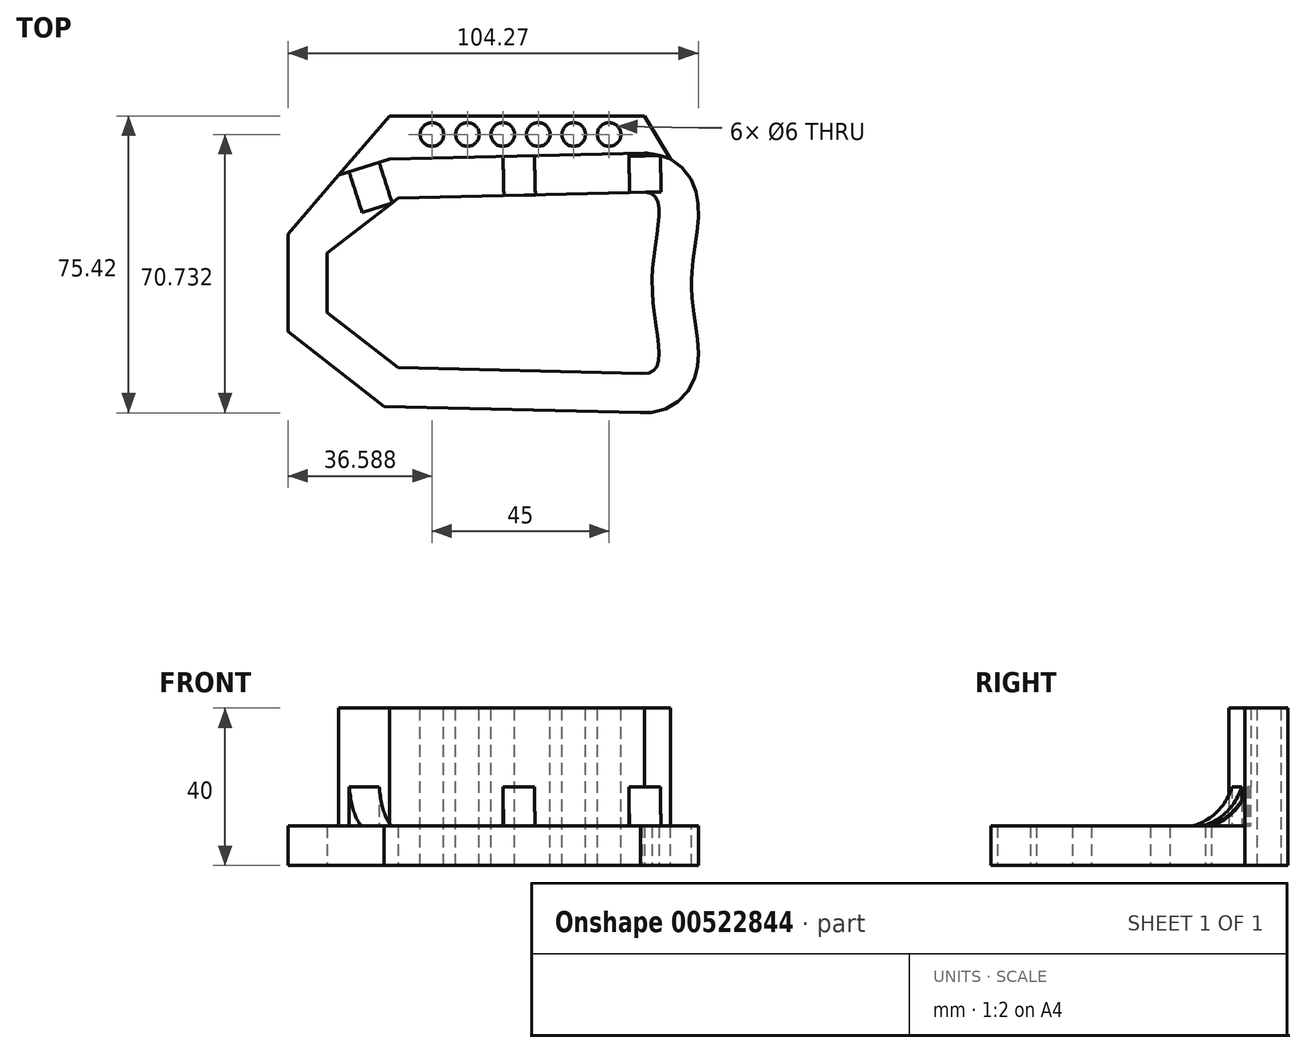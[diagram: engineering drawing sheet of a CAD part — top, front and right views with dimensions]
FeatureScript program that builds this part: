
annotation { "Feature Type Name" : "Feature", "Feature Type Description" : "" }
export const myFeature = defineFeature(function(context is Context, id is Id, definition is map)
    precondition{}
    {
        {
            var Q0;
            Q0=qCreatedBy(makeId("Top.planeOp"),FACE);
            var sketch = newSketch(context, id + "F0", { "sketchPlane" : qUnion([Q0])});
            skPoint(sketch, "E0.middle", {"position": v(0, 0) * mm});
            skLineSegment(sketch, "E1", {"start": v(-22, 21.5) * mm, "end": v(40, 23) * mm});
            skLineSegment(sketch, "E2", {"start": v(-22, -21.5) * mm, "end": v(40, -23) * mm});
            skLineSegment(sketch, "E3.bottom", {"start": v(-40, -7.5) * mm, "end": v(-40, -7.5) * mm});
            skLineSegment(sketch, "E3.top", {"start": v(-40, 7.5) * mm, "end": v(-40, 7.5) * mm});
            skLineSegment(sketch, "E3.left", {"start": v(-40, -7.5) * mm, "end": v(-40, 7.5) * mm});
            skLineSegment(sketch, "E3.right", {"start": v(-40, 7.5) * mm, "end": v(-40, -7.5) * mm});
            skPoint(sketch, "E3.middle", {"position": v(-40, 0) * mm});
            skLineSegment(sketch, "E4", {"start": v(-22, 21.5) * mm, "end": v(-40, 7.5) * mm});
            skLineSegment(sketch, "E5", {"start": v(-40, -7.5) * mm, "end": v(-22, -21.5) * mm});
            skFitSpline(sketch, "E6", {"points": [v(40, 23) * mm, v(42.5, 0) * mm, v(40, -23) * mm], "startDerivative": vector(46.5, 3.2) * mm, "endDerivative": vector(-46.5, 3.2) * mm});
            skPoint(sketch, "E0.right.end.orphan", {"position": v(40, 0) * mm});
            skLineSegment(sketch, "E7.1", {"start": v(-25.54, -31.42) * mm, "end": v(40.59, -33.02) * mm});
            skLineSegment(sketch, "E7.2", {"start": v(-50, -12.4) * mm, "end": v(-25.54, -31.42) * mm});
            skFitSpline(sketch, "E7.3", {"points": [v(39.31, 32.98) * mm, v(39.86, 33.01) * mm, v(40.99, 33.04) * mm, v(42.81, 32.89) * mm, v(44.75, 32.46) * mm, v(46.75, 31.69) * mm, v(48.68, 30.53) * mm, v(50.37, 29.06) * mm, v(51.7, 27.4) * mm, v(52.68, 25.7) * mm, v(53.34, 24.07) * mm, v(53.77, 22.55) * mm, v(54.03, 21.15) * mm, v(54.22, 19.42) * mm, v(54.26, 17.47) * mm, v(54.14, 15.3) * mm, v(53.93, 13.24) * mm, v(53.66, 11.23) * mm, v(53.38, 9.25) * mm, v(53.1, 7.29) * mm, v(52.86, 5.37) * mm, v(52.7, 3.8) * mm, v(52.6, 2.6) * mm, v(52.54, 1.7) * mm, v(52.51, 0.98) * mm, v(52.5, 0.41) * mm, v(52.5, 0) * mm, v(52.5, -0.41) * mm, v(52.51, -0.98) * mm, v(52.54, -1.7) * mm, v(52.6, -2.6) * mm, v(52.7, -3.8) * mm, v(52.86, -5.37) * mm, v(53.1, -7.29) * mm, v(53.38, -9.25) * mm, v(53.66, -11.23) * mm, v(53.93, -13.24) * mm, v(54.14, -15.3) * mm, v(54.26, -17.47) * mm, v(54.22, -19.42) * mm, v(54.03, -21.15) * mm, v(53.77, -22.55) * mm, v(53.34, -24.07) * mm, v(52.68, -25.7) * mm, v(51.7, -27.4) * mm, v(50.36, -29.06) * mm, v(48.68, -30.53) * mm, v(46.75, -31.69) * mm, v(44.75, -32.46) * mm, v(42.8, -32.89) * mm, v(40.99, -33.04) * mm, v(39.86, -33.01) * mm, v(39.31, -32.98) * mm]});
            skLineSegment(sketch, "E7.4", {"start": v(-50, 12.4) * mm, "end": v(-50, -12.4) * mm});
            skLineSegment(sketch, "E8.top", {"start": v(-24.21, 42.38) * mm, "end": v(40.59, 42.38) * mm});
            skPoint(sketch, "E9.top.end.orphan", {"position": v(22, 21.5) * mm});
            skPoint(sketch, "E9.bottom.end.orphan", {"position": v(22, -21.5) * mm});
            skLineSegment(sketch, "E10.trimOffspring", {"start": v(-40, 7.5) * mm, "end": v(-40, 0) * mm});
            skPoint(sketch, "E0.left.start.orphan", {"position": v(-40, 23) * mm});
            skPoint(sketch, "E11.trimOffspring.end.orphan", {"position": v(-40, -23) * mm});
            skLineSegment(sketch, "E12", {"start": v(40.59, 42.38) * mm, "end": v(47.14, 31.42) * mm});
            skLineSegment(sketch, "E13", {"start": v(-24.21, 42.38) * mm, "end": v(-50, 12.4) * mm});
            skPoint(sketch, "E14.start.orphan", {"position": v(-25.54, 31.42) * mm});
            skPoint(sketch, "E15.orphan", {"position": v(40.59, 33.02) * mm});
            skSolve(sketch);
        }
        {
            var Q0;
            Q0 = qSketchRegion(id + "F0", true);
            extrude(context, id + "F1", {"entities" : qUnion([Q0]), "depth" : 10 * mm, "offsetDistance" : 25 * mm});
        }
        {
            var Q0;
            Q0=makeQuery(id+"F1.opExtrude","CAP_FACE",FACE,{"disambiguationData":[OSD([sQuery(id+"F0.wireOp",EDGE,"E1"),sQuery(id+"F0.wireOp",EDGE,"E2"),sQuery(id+"F0.wireOp",EDGE,"E3.right"),sQuery(id+"F0.wireOp",EDGE,"E4"),sQuery(id+"F0.wireOp",EDGE,"E5"),sQuery(id+"F0.wireOp",EDGE,"E6"),sQuery(id+"F0.wireOp",EDGE,"E7.1"),sQuery(id+"F0.wireOp",EDGE,"E7.2"),sQuery(id+"F0.wireOp",EDGE,"E7.3"),sQuery(id+"F0.wireOp",EDGE,"E7.4"),sQuery(id+"F0.wireOp",EDGE,"E8.top"),sQuery(id+"F0.wireOp",EDGE,"E10.trimOffspring"),sQuery(id+"F0.wireOp",EDGE,"E12"),sQuery(id+"F0.wireOp",EDGE,"E13")])],"isStart":false});
            var sketch = newSketch(context, id + "F2", { "sketchPlane" : qUnion([Q0])});
            skLineSegment(sketch, "E16.bottom", {"start": v(-24.21, 42.38) * mm, "end": v(40.59, 42.38) * mm});
            skLineSegment(sketch, "E16.top", {"start": v(-24.21, 31.5) * mm, "end": v(40.59, 33) * mm});
            skFitSpline(sketch, "E17", {"points": [v(40.59, 33) * mm, v(47.14, 31.42) * mm, v(50.41, 28.91) * mm, v(51.97, 26.89) * mm], "startDerivative": vector(17.08, -2.64) * mm, "endDerivative": vector(6.98, -10.23) * mm});
            skLineSegment(sketch, "E18", {"start": v(47.14, 31.42) * mm, "end": v(40.59, 42.38) * mm});
            skLineSegment(sketch, "E19", {"start": v(-24.21, 31.5) * mm, "end": v(-37.1, 27.39) * mm});
            skLineSegment(sketch, "E20", {"start": v(-37.1, 27.39) * mm, "end": v(-24.21, 42.38) * mm});
            skSolve(sketch);
        }
        {
            var Q0;
            Q0=makeQuery(id+"F2.imprint","IMPRINT",FACE,{"disambiguationData":[TD([[makeQuery(id+"F2.imprint","IMPRINT",EDGE,{"derivedFrom":sQuery(id+"F2.wireOp",EDGE,"E16.bottom")}),-1.0]])]});
            extrude(context, id + "F3", {"entities" : qUnion([Q0]), "operationType" : NewBodyOperationType.ADD, "depth" : 30 * mm, "offsetDistance" : 25 * mm});
        }
        {
            var Q0;
            Q0=makeQuery(id+"F3.opExtrude","CAP_FACE",FACE,{"disambiguationData":[OSD([sQuery(id+"F2.wireOp",EDGE,"E16.bottom"),sQuery(id+"F2.wireOp",EDGE,"E16.top"),sQuery(id+"F2.wireOp",EDGE,"E17"),sQuery(id+"F2.wireOp",EDGE,"E18"),sQuery(id+"F2.wireOp",EDGE,"E19"),sQuery(id+"F2.wireOp",EDGE,"E20")])],"isStart":false});
            var sketch = newSketch(context, id + "F4", { "sketchPlane" : qUnion([Q0])});
            skLineSegment(sketch, "E21", {"start": v(-22.41, 37.7) * mm, "end": v(40.59, 37.7) * mm});
            skPoint(sketch, "E22.orphan", {"position": v(-20.61, 43.88) * mm});
            skPoint(sketch, "E23.start.orphan", {"position": v(-24.21, 31.5) * mm});
            skPoint(sketch, "E24.orphan", {"position": v(40.59, 33) * mm});
            skPoint(sketch, "E25.start.orphan", {"position": v(40.59, 42.38) * mm});
            skCircle(sketch, "E26", {"center": v(-13.41, 37.7) * mm, "radius": 3 * mm});
            skCircle(sketch, "E27", {"center": v(-4.41, 37.7) * mm, "radius": 3 * mm});
            skCircle(sketch, "E28", {"center": v(4.59, 37.7) * mm, "radius": 3 * mm});
            skCircle(sketch, "E29", {"center": v(13.59, 37.7) * mm, "radius": 3 * mm});
            skCircle(sketch, "E30", {"center": v(22.59, 37.7) * mm, "radius": 3 * mm});
            skCircle(sketch, "E31", {"center": v(31.59, 37.7) * mm, "radius": 3 * mm});
            skSolve(sketch);
        }
        {
            var Q0;
            Q0 = qSketchRegion(id + "F4", true);
            extrude(context, id + "F5", {"entities" : qUnion([Q0]), "operationType" : NewBodyOperationType.REMOVE, "oppositeDirection" : true, "depth" : 43 * mm, "offsetDistance" : 25 * mm});
        }
        {
            var Q0;
            Q0=makeQuery(id+"F3.opExtrude","SWEPT_FACE",FACE,{"disambiguationData":[OSD([sQuery(id+"F2.wireOp",EDGE,"E16.top")])]});
            var sketch = newSketch(context, id + "F6", { "sketchPlane" : qUnion([Q0])});
            skLineSegment(sketch, "E32.bottom", {"start": v(13.36, 20) * mm, "end": v(5.36, 20) * mm});
            skLineSegment(sketch, "E32.left", {"start": v(13.36, 20) * mm, "end": v(13.36, 10) * mm});
            skLineSegment(sketch, "E32.right", {"start": v(5.36, 20) * mm, "end": v(5.36, 10) * mm});
            skPoint(sketch, "E32.middle", {"position": v(8.93, 10) * mm});
            skLineSegment(sketch, "E33", {"start": v(5.36, 10) * mm, "end": v(13.36, 10) * mm});
            skSolve(sketch);
        }
        {
            var Q0;
            Q0 = qSketchRegion(id + "F6", true);
            extrude(context, id + "F7", {"entities" : qUnion([Q0]), "operationType" : NewBodyOperationType.ADD, "depth" : 10 * mm, "offsetDistance" : 25 * mm});
        }
        {
            var Q0;
            Q0=makeQuery(id+"F7.opExtrude","SWEPT_FACE",FACE,{"disambiguationData":[OSD([sQuery(id+"F6.wireOp",EDGE,"E32.right")])]});
            var sketch = newSketch(context, id + "F8", { "sketchPlane" : qUnion([Q0])});
            skArc(sketch, "E34", {"start": v(-32.05, 20) * mm, "mid": v(-28.3, 13.75) * mm, "end": v(-22.05, 10) * mm});
            skLineSegment(sketch, "E35", {"start": v(-32.05, 20) * mm, "end": v(-22.05, 20) * mm});
            skLineSegment(sketch, "E36", {"start": v(-22.05, 20) * mm, "end": v(-22.05, 10) * mm});
            skSolve(sketch);
        }
        {
            var Q0;
            Q0 = qSketchRegion(id + "F8", true);
            extrude(context, id + "F9", {"entities" : qUnion([Q0]), "operationType" : NewBodyOperationType.REMOVE, "oppositeDirection" : true, "depth" : 25 * mm, "offsetDistance" : 25 * mm});
        }
        {
            var Q0;
            Q0=makeQuery(id+"F3.opExtrude","SWEPT_FACE",FACE,{"disambiguationData":[OSD([sQuery(id+"F2.wireOp",EDGE,"E19")])]});
            var sketch = newSketch(context, id + "F10", { "sketchPlane" : qUnion([Q0])});
            skLineSegment(sketch, "E37.bottom", {"start": v(-24.26, 20) * mm, "end": v(-16.26, 20) * mm});
            skLineSegment(sketch, "E37.left", {"start": v(-24.26, 20) * mm, "end": v(-24.26, 10) * mm});
            skLineSegment(sketch, "E37.right", {"start": v(-16.26, 20) * mm, "end": v(-16.26, 10) * mm});
            skPoint(sketch, "E37.middle", {"position": v(-20.26, 10) * mm});
            skLineSegment(sketch, "E38", {"start": v(-24.26, 10) * mm, "end": v(-16.26, 10) * mm});
            skSolve(sketch);
        }
        {
            var Q0;
            Q0 = qSketchRegion(id + "F10", true);
            extrude(context, id + "F11", {"entities" : qUnion([Q0]), "operationType" : NewBodyOperationType.ADD, "depth" : 10.87 * mm, "offsetDistance" : 25 * mm});
        }
        {
            var Q0;
            Q0=makeQuery(id+"F11.opExtrude","SWEPT_FACE",FACE,{"disambiguationData":[OSD([sQuery(id+"F10.wireOp",EDGE,"E37.left")])]});
            var sketch = newSketch(context, id + "F12", { "sketchPlane" : qUnion([Q0])});
            skArc(sketch, "E39", {"start": v(-37.37, 20) * mm, "mid": v(-33.25, 13.57) * mm, "end": v(-26.5, 10) * mm});
            skSolve(sketch);
        }
        {
            var Q0;
            Q0 = qSketchRegion(id + "F12", true);
            var Q1;
            Q1=makeQuery(id+"F12.imprint","IMPRINT",FACE,{"disambiguationData":[TD([[makeQuery(id+"F12.imprint","IMPRINT",EDGE,{"derivedFrom":sQuery(id+"F12.wireOp",EDGE,"E39")}),1.0]])]});
            extrude(context, id + "F13", {"entities" : qUnion([Q0, Q1]), "operationType" : NewBodyOperationType.REMOVE, "oppositeDirection" : true, "depth" : 8.3 * mm, "offsetDistance" : 25 * mm});
        }
        {
            var Q0;
            Q0=makeQuery(id+"F3.opExtrude","SWEPT_FACE",FACE,{"disambiguationData":[OSD([sQuery(id+"F2.wireOp",EDGE,"E16.top")])]});
            var sketch = newSketch(context, id + "F14", { "sketchPlane" : qUnion([Q0])});
            skLineSegment(sketch, "E40.bottom", {"start": v(37.34, 20) * mm, "end": v(45.34, 20) * mm});
            skLineSegment(sketch, "E40.left", {"start": v(37.34, 20) * mm, "end": v(37.34, 10) * mm});
            skLineSegment(sketch, "E40.right", {"start": v(45.34, 20) * mm, "end": v(45.34, 10) * mm});
            skPoint(sketch, "E40.middle", {"position": v(41.34, 10) * mm});
            skLineSegment(sketch, "E41", {"start": v(37.34, 10) * mm, "end": v(45.34, 10) * mm});
            skSolve(sketch);
        }
        {
            var Q0;
            Q0 = qSketchRegion(id + "F14", true);
            extrude(context, id + "F15", {"entities" : qUnion([Q0]), "operationType" : NewBodyOperationType.ADD, "depth" : 10 * mm, "offsetDistance" : 25 * mm});
        }
        {
            var Q0;
            Q0=makeQuery(id+"F15.opExtrude","SWEPT_FACE",FACE,{"disambiguationData":[OSD([sQuery(id+"F14.wireOp",EDGE,"E40.right")])]});
            var sketch = newSketch(context, id + "F16", { "sketchPlane" : qUnion([Q0])});
            skArc(sketch, "E42", {"start": v(22.05, 10) * mm, "mid": v(27.84, 13.9) * mm, "end": v(31.24, 20) * mm});
            skLineSegment(sketch, "E43", {"start": v(31.24, 20) * mm, "end": v(22.05, 20) * mm});
            skLineSegment(sketch, "E44", {"start": v(22.05, 20) * mm, "end": v(22.05, 10) * mm});
            skSolve(sketch);
        }
        {
            var Q0;
            Q0 = qSketchRegion(id + "F16", true);
            extrude(context, id + "F17", {"entities" : qUnion([Q0]), "operationType" : NewBodyOperationType.REMOVE, "oppositeDirection" : true, "depth" : 9.2 * mm, "offsetDistance" : 25 * mm});
        }
    });
